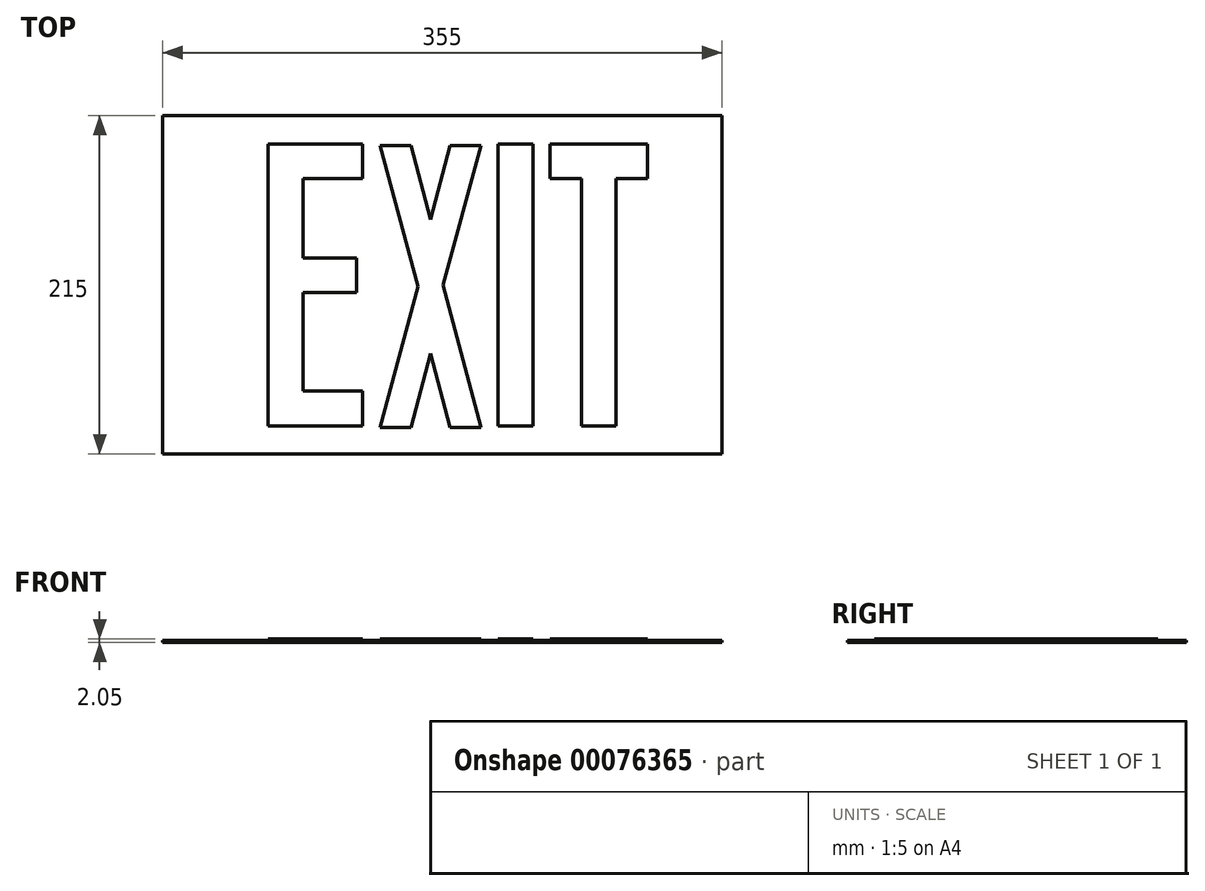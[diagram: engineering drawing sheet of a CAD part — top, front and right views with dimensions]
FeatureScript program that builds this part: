
annotation { "Feature Type Name" : "Feature", "Feature Type Description" : "" }
export const myFeature = defineFeature(function(context is Context, id is Id, definition is map)
    precondition{}
    {
        {
            var Q0;
            Q0=qCreatedBy(makeId("Top.planeOp"),FACE);
            var sketch = newSketch(context, id + "F0", { "sketchPlane" : qUnion([Q0])});
            skLineSegment(sketch, "E0.bottom", {"start": v(177.5, 107.5) * mm, "end": v(-177.5, 107.5) * mm});
            skLineSegment(sketch, "E0.top", {"start": v(177.5, -107.5) * mm, "end": v(-177.5, -107.5) * mm});
            skLineSegment(sketch, "E0.left", {"start": v(177.5, 107.5) * mm, "end": v(177.5, -107.5) * mm});
            skLineSegment(sketch, "E0.right", {"start": v(-177.5, 107.5) * mm, "end": v(-177.5, -107.5) * mm});
            skPoint(sketch, "E0.middle", {"position": v(0, 0) * mm});
            skSolve(sketch);
        }
        {
            var Q0;
            Q0 = qSketchRegion(id + "F0", true);
            extrude(context, id + "F1", {"entities" : qUnion([Q0]), "depth" : 1.1 * mm});
        }
        {
            var Q0;
            Q0=makeQuery(id+"F1.opExtrude","CAP_FACE",FACE,{"disambiguationData":[OSD([sQuery(id+"F0.wireOp",EDGE,"E0.bottom"),sQuery(id+"F0.wireOp",EDGE,"E0.top"),sQuery(id+"F0.wireOp",EDGE,"E0.left"),sQuery(id+"F0.wireOp",EDGE,"E0.right")])],"isStart":false});
            var sketch = newSketch(context, id + "F2", { "sketchPlane" : qUnion([Q0])});
            skLineSegment(sketch, "E1.bottom", {"start": v(-110.5, 89.5) * mm, "end": v(-88.5, 89.5) * mm});
            skLineSegment(sketch, "E1.top", {"start": v(-110.5, -89.5) * mm, "end": v(-88.5, -89.5) * mm});
            skLineSegment(sketch, "E1.left", {"start": v(-110.5, 89.5) * mm, "end": v(-110.5, -89.5) * mm});
            skLineSegment(sketch, "E1.right", {"start": v(-88.5, 89.5) * mm, "end": v(-88.5, -89.5) * mm});
            skLineSegment(sketch, "E2.bottom", {"start": v(-88.5, 89.5) * mm, "end": v(-50.5, 89.5) * mm});
            skLineSegment(sketch, "E2.top", {"start": v(-88.5, 67.5) * mm, "end": v(-50.5, 67.5) * mm});
            skLineSegment(sketch, "E2.left", {"start": v(-88.5, 89.5) * mm, "end": v(-88.5, 67.5) * mm});
            skLineSegment(sketch, "E2.right", {"start": v(-50.5, 89.5) * mm, "end": v(-50.5, 67.5) * mm});
            skLineSegment(sketch, "E3.bottom", {"start": v(-88.5, -89.5) * mm, "end": v(-50.5, -89.5) * mm});
            skLineSegment(sketch, "E3.top", {"start": v(-88.5, -67.5) * mm, "end": v(-50.5, -67.5) * mm});
            skLineSegment(sketch, "E3.left", {"start": v(-88.5, -89.5) * mm, "end": v(-88.5, -67.5) * mm});
            skLineSegment(sketch, "E3.right", {"start": v(-50.5, -89.5) * mm, "end": v(-50.5, -67.5) * mm});
            skLineSegment(sketch, "E4.bottom", {"start": v(-88.5, 17.01) * mm, "end": v(-54.5, 17.01) * mm});
            skLineSegment(sketch, "E4.top", {"start": v(-88.5, -4.99) * mm, "end": v(-54.5, -4.99) * mm});
            skLineSegment(sketch, "E4.left", {"start": v(-88.5, 17.01) * mm, "end": v(-88.5, -4.99) * mm});
            skLineSegment(sketch, "E4.right", {"start": v(-54.5, 17.01) * mm, "end": v(-54.5, -4.99) * mm});
            skSolve(sketch);
        }
        {
            var Q0;
            Q0 = qSketchRegion(id + "F2", true);
            extrude(context, id + "F3", {"entities" : qUnion([Q0]), "operationType" : NewBodyOperationType.ADD, "depth" : .95 * mm});
        }
        {
            var Q0;
            Q0=makeQuery(id+"F1.opExtrude","CAP_FACE",FACE,{"disambiguationData":[OSD([sQuery(id+"F0.wireOp",EDGE,"E0.bottom"),sQuery(id+"F0.wireOp",EDGE,"E0.top"),sQuery(id+"F0.wireOp",EDGE,"E0.left"),sQuery(id+"F0.wireOp",EDGE,"E0.right")])],"isStart":false});
            var sketch = newSketch(context, id + "F4", { "sketchPlane" : qUnion([Q0])});
            skLineSegment(sketch, "E5.bottom", {"start": v(68.5, 89.5) * mm, "end": v(130.5, 89.5) * mm});
            skLineSegment(sketch, "E5.top", {"start": v(68.5, 67.5) * mm, "end": v(130.5, 67.5) * mm});
            skLineSegment(sketch, "E5.left", {"start": v(68.5, 89.5) * mm, "end": v(68.5, 67.5) * mm});
            skLineSegment(sketch, "E5.right", {"start": v(130.5, 89.5) * mm, "end": v(130.5, 67.5) * mm});
            skLineSegment(sketch, "E6.bottom", {"start": v(88.5, 67.5) * mm, "end": v(110.5, 67.5) * mm});
            skLineSegment(sketch, "E6.top", {"start": v(88.5, -89.5) * mm, "end": v(110.5, -89.5) * mm});
            skLineSegment(sketch, "E6.left", {"start": v(88.5, 67.5) * mm, "end": v(88.5, -89.5) * mm});
            skLineSegment(sketch, "E6.right", {"start": v(110.5, 67.5) * mm, "end": v(110.5, -89.5) * mm});
            skSolve(sketch);
        }
        {
            var Q0;
            Q0 = qSketchRegion(id + "F4", true);
            extrude(context, id + "F5", {"entities" : qUnion([Q0]), "operationType" : NewBodyOperationType.ADD, "depth" : .95 * mm});
        }
        {
            var Q0;
            Q0=makeQuery(id+"F1.opExtrude","CAP_FACE",FACE,{"disambiguationData":[OSD([sQuery(id+"F0.wireOp",EDGE,"E0.bottom"),sQuery(id+"F0.wireOp",EDGE,"E0.top"),sQuery(id+"F0.wireOp",EDGE,"E0.left"),sQuery(id+"F0.wireOp",EDGE,"E0.right")])],"isStart":false});
            var sketch = newSketch(context, id + "F6", { "sketchPlane" : qUnion([Q0])});
            skLineSegment(sketch, "E7.bottom", {"start": v(35.5, 89.5) * mm, "end": v(57.5, 89.5) * mm});
            skLineSegment(sketch, "E7.top", {"start": v(35.5, -89.5) * mm, "end": v(57.5, -89.5) * mm});
            skLineSegment(sketch, "E7.left", {"start": v(35.5, 89.5) * mm, "end": v(35.5, -89.5) * mm});
            skLineSegment(sketch, "E7.right", {"start": v(57.5, 89.5) * mm, "end": v(57.5, -89.5) * mm});
            skSolve(sketch);
        }
        {
            var Q0;
            Q0 = qSketchRegion(id + "F6", true);
            extrude(context, id + "F7", {"entities" : qUnion([Q0]), "operationType" : NewBodyOperationType.ADD, "depth" : .95 * mm});
        }
        {
            var Q0;
            Q0=makeQuery(id+"F1.opExtrude","CAP_FACE",FACE,{"disambiguationData":[OSD([sQuery(id+"F0.wireOp",EDGE,"E0.bottom"),sQuery(id+"F0.wireOp",EDGE,"E0.top"),sQuery(id+"F0.wireOp",EDGE,"E0.left"),sQuery(id+"F0.wireOp",EDGE,"E0.right")])],"isStart":false});
            var sketch = newSketch(context, id + "F8", { "sketchPlane" : qUnion([Q0])});
            skLineSegment(sketch, "E8.bottom", {"start": v(-39.5, 88.5) * mm, "end": v(24.5, 88.5) * mm});
            skLineSegment(sketch, "E8.top", {"start": v(-39.5, -90.5) * mm, "end": v(24.5, -90.5) * mm});
            skLineSegment(sketch, "E8.left", {"start": v(-39.5, 88.5) * mm, "end": v(-39.5, -90.5) * mm});
            skLineSegment(sketch, "E8.right", {"start": v(24.5, 88.5) * mm, "end": v(24.5, -90.5) * mm});
            skSolve(sketch);
        }
        {
            var Q0;
            Q0 = qSketchRegion(id + "F8", true);
            extrude(context, id + "F9", {"entities" : qUnion([Q0]), "operationType" : NewBodyOperationType.ADD, "depth" : .95 * mm});
        }
        {
            var Q0;
            Q0=makeQuery(id+"F9.opExtrude","CAP_FACE",FACE,{"disambiguationData":[OSD([sQuery(id+"F8.wireOp",EDGE,"E8.bottom"),sQuery(id+"F8.wireOp",EDGE,"E8.top"),sQuery(id+"F8.wireOp",EDGE,"E8.left"),sQuery(id+"F8.wireOp",EDGE,"E8.right")])],"isStart":false});
            var sketch = newSketch(context, id + "F10", { "sketchPlane" : qUnion([Q0])});
            skLineSegment(sketch, "E9", {"start": v(-7.5, 119.34) * mm, "end": v(-7.5, -121.98) * mm, "construction": true});
            skLineSegment(sketch, "E10", {"start": v(-50.5, -1) * mm, "end": v(29.4, -1) * mm, "construction": true});
            skLineSegment(sketch, "E11", {"start": v(-39.5, 88.5) * mm, "end": v(-15.5, -1) * mm});
            skLineSegment(sketch, "E12", {"start": v(-15.5, -1) * mm, "end": v(-39.5, -90.5) * mm});
            skSolve(sketch);
        }
        {
            var Q0;
            Q0=makeQuery(id+"F10.imprint","IMPRINT",FACE,{"disambiguationData":[TD([[makeQuery(id+"F10.imprint","IMPRINT",EDGE,{"derivedFrom":sQuery(id+"F10.wireOp",EDGE,"E11")}),-1.0]])]});
            extrude(context, id + "F11", {"entities" : qUnion([Q0]), "operationType" : NewBodyOperationType.REMOVE, "oppositeDirection" : true, "depth" : .95 * mm});
        }
        {
            var Q0;
            Q0=makeQuery(id+"F9.opExtrude","CAP_FACE",FACE,{"disambiguationData":[OSD([sQuery(id+"F8.wireOp",EDGE,"E8.bottom"),sQuery(id+"F8.wireOp",EDGE,"E8.top"),sQuery(id+"F8.wireOp",EDGE,"E8.left"),sQuery(id+"F8.wireOp",EDGE,"E8.right")])],"isStart":false});
            var sketch = newSketch(context, id + "F12", { "sketchPlane" : qUnion([Q0])});
            skLineSegment(sketch, "E13", {"start": v(24.5, 88.5) * mm, "end": v(0.5, 0) * mm});
            skLineSegment(sketch, "E14", {"start": v(0.5, 0) * mm, "end": v(24.5, -90.5) * mm});
            skSolve(sketch);
        }
        {
            var Q0;
            Q0=makeQuery(id+"F12.imprint","IMPRINT",FACE,{"disambiguationData":[TD([[makeQuery(id+"F12.imprint","IMPRINT",EDGE,{"derivedFrom":sQuery(id+"F12.wireOp",EDGE,"E13")}),1.0]])]});
            extrude(context, id + "F13", {"entities" : qUnion([Q0]), "operationType" : NewBodyOperationType.REMOVE, "oppositeDirection" : true, "depth" : .95 * mm});
        }
        {
            var Q0;
            Q0=makeQuery(id+"F9.opExtrude","CAP_FACE",FACE,{"disambiguationData":[OSD([sQuery(id+"F8.wireOp",EDGE,"E8.bottom"),sQuery(id+"F8.wireOp",EDGE,"E8.top"),sQuery(id+"F8.wireOp",EDGE,"E8.left"),sQuery(id+"F8.wireOp",EDGE,"E8.right")])],"isStart":false});
            var sketch = newSketch(context, id + "F14", { "sketchPlane" : qUnion([Q0])});
            skLineSegment(sketch, "E15", {"start": v(-19.85, -90.5) * mm, "end": v(-7.5, -43.5) * mm});
            skLineSegment(sketch, "E16", {"start": v(-7.5, -43.5) * mm, "end": v(4.85, -90.5) * mm});
            skLineSegment(sketch, "E17", {"start": v(4.85, -90.5) * mm, "end": v(-19.85, -90.5) * mm});
            skSolve(sketch);
        }
        {
            var Q0;
            Q0 = qSketchRegion(id + "F14", true);
            extrude(context, id + "F15", {"entities" : qUnion([Q0]), "operationType" : NewBodyOperationType.REMOVE, "oppositeDirection" : true, "depth" : .95 * mm});
        }
        {
            var Q0;
            Q0=makeQuery(id+"F9.opExtrude","CAP_FACE",FACE,{"disambiguationData":[OSD([sQuery(id+"F8.wireOp",EDGE,"E8.bottom"),sQuery(id+"F8.wireOp",EDGE,"E8.top"),sQuery(id+"F8.wireOp",EDGE,"E8.left"),sQuery(id+"F8.wireOp",EDGE,"E8.right")])],"isStart":false});
            var sketch = newSketch(context, id + "F16", { "sketchPlane" : qUnion([Q0])});
            skLineSegment(sketch, "E18", {"start": v(-19.85, 88.5) * mm, "end": v(-7.5, 41.5) * mm});
            skLineSegment(sketch, "E19", {"start": v(-7.5, 41.5) * mm, "end": v(4.85, 88.5) * mm});
            skLineSegment(sketch, "E20", {"start": v(4.85, 88.5) * mm, "end": v(-19.85, 88.5) * mm});
            skSolve(sketch);
        }
        {
            var Q0;
            Q0 = qSketchRegion(id + "F16", true);
            extrude(context, id + "F17", {"entities" : qUnion([Q0]), "operationType" : NewBodyOperationType.REMOVE, "oppositeDirection" : true, "depth" : .95 * mm});
        }
    });
